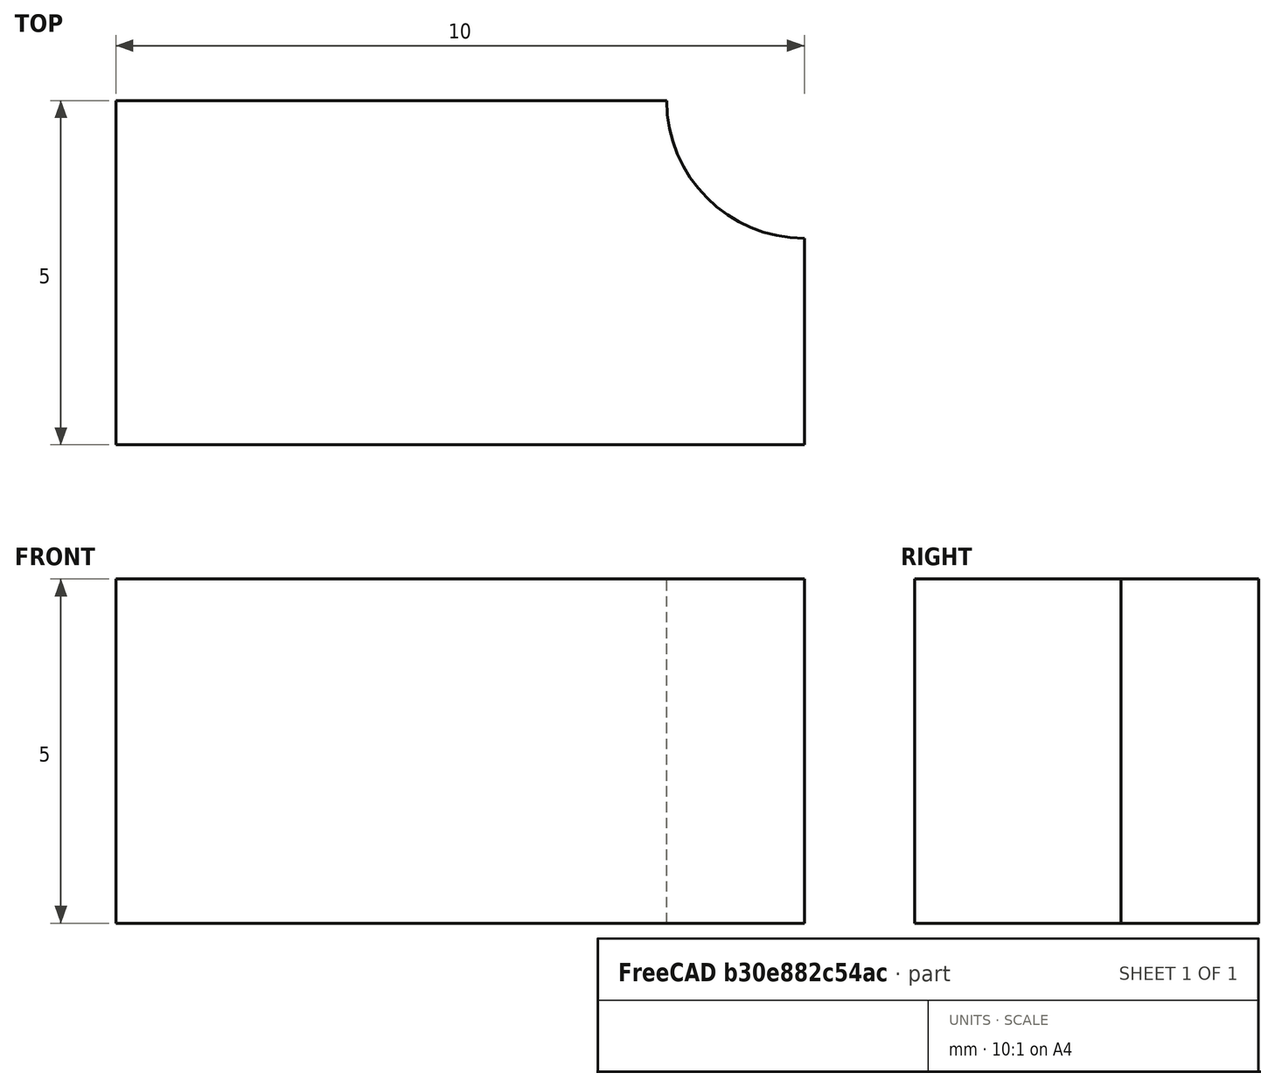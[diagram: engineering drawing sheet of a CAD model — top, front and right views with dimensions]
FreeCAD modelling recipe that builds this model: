
FCSTD DOCUMENT  (FreeCAD 0.17R8470 (Git))
Label: Linear
License: All rights reserved
LicenseURL: http://en.wikipedia.org/wiki/All_rights_reserved
objects: Fem::ConstraintDisplacement×2, Part::Box×1, Part::Cylinder×1, Part::Cut×1, Fem::FemSolverObjectPython×1, Fem::FemMeshShapeNetgenObject×1, Fem::ConstraintPressure×1, Fem::ConstraintFixed×1, App::MaterialObjectPython×1, Fem::FemResultObject×1, Fem::FemAnalysisPython×1
note: 3 computed .brp shape members not serialized (recipe doc carries the construction recipe); baked Part::Feature solids carry a one-line shape summary decoded from their .brp

FEATURE [Part::Box] Box  label="Cube"
  AttacherType = Attacher::AttachEngine3D
  Height = 5
  Length = 10
  Width = 5
FEATURE [Part::Cylinder] Cylinder
  Angle = 360
  AttacherType = Attacher::AttachEngine3D
  Height = 5
  Placement = pos=(10,5,0) rot=(0,0,1;0rad)
  Radius = 2
FEATURE [Part::Cut] Cut
  Base = -> Box
  Tool = -> Cylinder
FEATURE [Fem::FemSolverObjectPython] CalculiX  # FEM object (typed FeaturePython)
  AnalysisType = 0
  EigenmodeHighLimit = 1000000
  EigenmodeLowLimit = 0
  EigenmodesCount = 10
  GeometricalNonlinearity = 0
  IterationsControlParameterCutb = 0.25,0.5,0.75,0.85,,,1.5,
  IterationsControlParameterIter = 4,8,9,200,10,400,,200,,
  IterationsControlParameterTimeUse = false
  IterationsMaximum = 2000
  MatrixSolverType = 0
  SolverType = FemSolverCalculix
  SteadyState = true
  TimeEnd = 1
  TimeInitialStep = 0.01
FEATURE [Fem::FemMeshShapeNetgenObject] Cut_Mesh
  Fineness = 2
  GrowthRate = 0.3
  MaxSize = 1000
  NbSegsPerEdge = 1
  NbSegsPerRadius = 2
  Optimize = true
  SecondOrder = true
  Shape = -> Cut
FEATURE [Fem::ConstraintDisplacement] FemConstraintDisplacement
  NormalDirection = (1,0,0)
  Normals = (9) [(1,0,0),(1,0,0),(1,0,0),(1,0,0),(1,0,0),(1,0,0),(1,0,0),(1,0,0),(1,0,0)]
  Points = (9) [(10,3,0),(10,3,2.5),(10,3,5),(10,1.5,0),(10,1.5,2.5),(10,1.5,5),(10,0,0),(10,0,2.5),(10,0,5)]
  References = -> [Cut]
  rotxFix = false
  rotxFree = true
  rotyFix = false
  rotyFree = true
  rotzFix = false
  rotzFree = true
  xDisplacement = 0
  xFix = true
  xFree = false
  xRotation = 0
  yDisplacement = 0
  yFix = false
  yFree = true
  yRotation = 0
  zDisplacement = 0
  zFix = false
  zFree = true
  zRotation = 0
FEATURE [Fem::ConstraintDisplacement] FemConstraintDisplacement001
  NormalDirection = (0,1,0)
  Normals = (9) [(0,1,0),(0,1,0),(0,1,0),(0,1,0),(0,1,0),(0,1,0),(0,1,0),(0,1,0),(0,1,0)]
  Points = (9) [(0,5,0),(0,5,2.5),(0,5,5),(4,5,0),(4,5,2.5),(4,5,5),(8,5,0),(8,5,2.5),(8,5,5)]
  References = -> [Cut]
  rotxFix = false
  rotxFree = true
  rotyFix = false
  rotyFree = true
  rotzFix = false
  rotzFree = true
  xDisplacement = 0
  xFix = false
  xFree = true
  xRotation = 0
  yDisplacement = 0
  yFix = true
  yFree = false
  yRotation = 0
  zDisplacement = 0
  zFix = false
  zFree = true
  zRotation = 0
FEATURE [Fem::ConstraintPressure] FemConstraintPressure
  NormalDirection = (-1,0,0)
  Normals = (9) [(-1,0,0),(-1,0,0),(-1,0,0),(-1,0,0),(-1,0,0),(-1,0,0),(-1,0,0),(-1,0,0),(-1,0,0)]
  Points = (9) [(0,5,0),(0,5,2.5),(0,5,5),(0,2.5,0),(0,2.5,2.5),(0,2.5,5),(0,0,0),(0,0,2.5),(0,0,5)]
  Pressure = 10
  References = -> [Cut]
  Reversed = true
FEATURE [Fem::ConstraintFixed] FemConstraintFixed
  NormalDirection = (0,0,1)
  Normals = (1) [(0,0,1)]
  Points = (1) [(10,0,0)]
  References = -> [Cut]
FEATURE [App::MaterialObjectPython] MechanicalMaterial  # material (typed FeaturePython)
  Material = Density=7900.0 kg/m^3,+10 more (map truncated)
FEATURE [Fem::FemResultObject] CalculiX_static_results
  DisplacementLengths = [0.000127539,0.000380277,0.000284989,0.000382015,0.000263235,0,0.000621989,0.000654622,0.000595632,0.000631714,0.000344248,0.000291556,0.000154179,0.000192672,0.000228091,0.000318496,0.000193678,0.000364996,0.000364948,0.000369263,+370 more]
  DisplacementVectors = (390) [(0,0.000117894,-4.86541e-05),(-0.000350981,0,-0.000146366),(0,0.000171452,-0.000227646),(-0.000362074,0,-0.00012181),(0,0.000214212,-0.000152989),+385 more]
  Eigenmode = 0
  EigenmodeFrequency = 0
  MaxShear = [14.0489,3.15283,14.9695,3.61304,4.51426,11.8982,5.10978,4.82226,5.06618,5.10989,3.27301,11.4468,16.3029,15.0688,17.1922,2.53848,11.3527,6.8653,7.34007,7.88983,7.13773,7.04392,6.05123,3.71082,2.16877,6.54521,6.7613,4.17347,2.03701,6.68365,+360 more]
  Mesh = -> Cut_Mesh
  NodeNumbers = [1,2,3,4,5,6,7,8,9,10,11,12,13,14,15,16,17,18,19,20,21,22,23,24,25,26,27,28,29,30,31,32,33,34,35,36,37,38,39,40,41,42,43,44,45,46,47,48,49,50,51,52,53,54,55,56,57,58,59,60,61,62,63,64,65,66,67,68,69,+321 more]
  PrincipalMax = [28.8445,-0.296882,30.7651,-0.247574,8.68258,21.3618,10.2293,9.77056,10.0183,10.0622,1.73161,21.9479,34.821,33.5803,36.7358,3.73026,22.2119,-0.264028,-0.503095,-0.256452,14.1043,13.7836,8.69346,7.59558,4.27819,12.9798,12.0181,8.39155,+362 more]
  PrincipalMed = [2.84172,-1.45853,2.24556,-1.57826,0.158347,8.91023,1.59851,1.34581,-0.0389486,0.0366118,-0.708165,1.08647,4.11838,5.25503,4.48211,-0.469021,1.16771,-3.73534,-4.93181,-3.98473,3.00612,7.82388,-0.843416,2.18154,2.32554,0.279355,-0.050131,+363 more]
  PrincipalMin = [0.746754,-6.60253,0.826144,-7.47365,-0.345933,-2.43471,0.00971928,0.126042,-0.114031,-0.157634,-4.81441,-0.945671,2.2152,3.44259,2.35133,-1.3467,-0.493481,-13.9946,-15.1832,-16.0361,-0.171178,-0.304203,-3.409,0.173945,-0.0593472,-0.110665,+364 more]
  Stats = [-0.000625856,-0.000224355,0,-1.51403e-06,7.47669e-05,0.000214212,-0.000227646,-0.000130162,0,0,0.000298199,0.000654622,1.91713,12.568,33.3701,-0.863561,11.8005,38.2562,-4.93181,0.633107,11.2484,-16.0361,-1.46902,3.72537,1.10142,6.63476,+1 more]
  StressValues = [27.1111,5.81255,29.2551,6.66117,8.78723,20.6158,9.52507,9.09618,10.095,10.1241,5.72993,21.9482,31.6971,29.2736,33.3701,4.69999,21.922,12.3659,13.0425,14.2852,12.9818,12.2485,11.0454,6.64917,3.76263,12.8998,12.8573,7.97195,3.62291,13.2197,+360 more]
  Temperature = [0]
  Time = 0
FEATURE [Fem::FemAnalysisPython] Analysis  # FEM object (typed FeaturePython)
  Member = -> [CalculiX,Cut_Mesh,FemConstraintDisplacement,FemConstraintDisplacement001,FemConstraintPressure,FemConstraintFixed,MechanicalMaterial,CalculiX_static_results]
